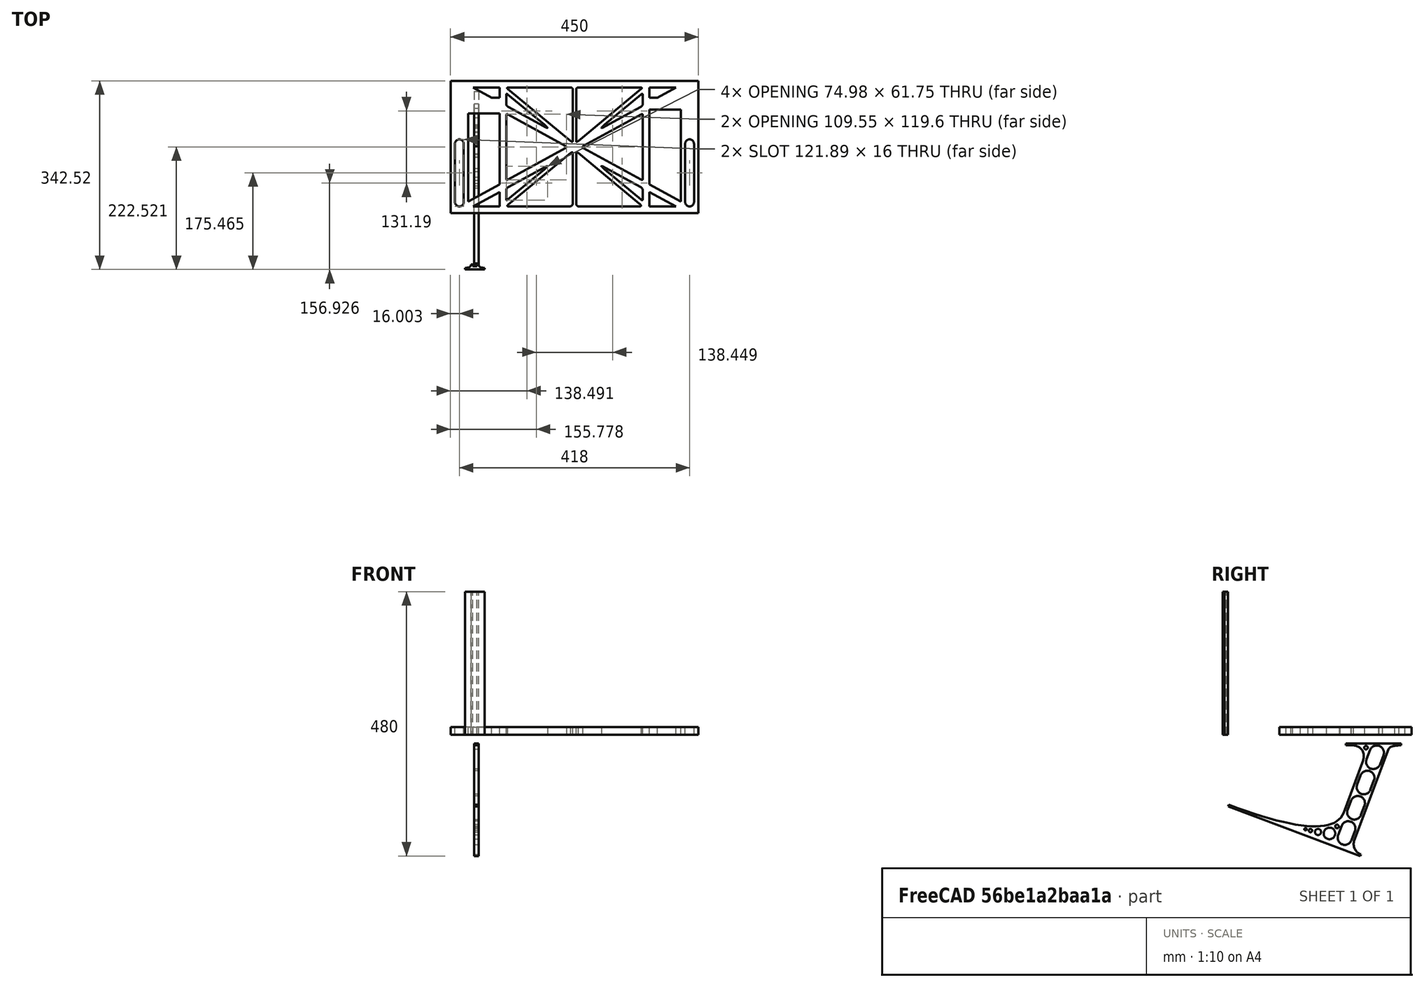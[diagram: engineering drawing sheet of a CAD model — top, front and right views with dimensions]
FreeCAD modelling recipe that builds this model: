
FCSTD DOCUMENT  (FreeCAD 0.19R0.19.2)
Label: laptopStand096
License: All rights reserved
LicenseURL: http://en.wikipedia.org/wiki/All_rights_reserved
objects: Sketcher::SketchObject×3, Part::Extrusion×3
note: 6 computed .brp shape members not serialized (recipe doc carries the construction recipe); baked Part::Feature solids carry a one-line shape summary decoded from their .brp

FEATURE [Sketcher::SketchObject] Sketch
  FullyConstrained = false
  sketch-geometry (252):
    g0: LineSegment StartX=-10.9272 StartY=-82.7794 StartZ=0 EndX=46.0728 EndY=-51.4823 EndZ=0
    g1: LineSegment StartX=366.073 StartY=-91.7794 StartZ=0 EndX=318.073 EndY=-65.424 EndZ=0
    g2: LineSegment StartX=-10.9272 StartY=77.3346 StartZ=0 EndX=-10.9272 EndY=-82.7794 EndZ=0
    g3: LineSegment StartX=375.073 StartY=-82.7794 StartZ=0 EndX=375.073 EndY=83.9235 EndZ=0
    g4: LineSegment StartX=-1.92719 StartY=-91.7794 StartZ=0 EndX=46.0728 EndY=-91.7794 EndZ=0
    g5: LineSegment StartX=318.073 StartY=124.221 StartZ=0 EndX=366.073 EndY=124.221 EndZ=0
    g6: LineSegment StartX=318.073 StartY=83.9235 StartZ=0 EndX=318.073 EndY=-51.4823 EndZ=0
    g7: LineSegment StartX=318.073 StartY=-51.4823 StartZ=0 EndX=375.073 EndY=-82.7794 EndZ=0
    g8: LineSegment StartX=318.073 StartY=-65.424 StartZ=0 EndX=318.073 EndY=-91.7794 EndZ=0
    g9: LineSegment StartX=318.073 StartY=-91.7794 StartZ=0 EndX=366.073 EndY=-91.7794 EndZ=0
    g10: LineSegment StartX=46.0728 StartY=-65.424 StartZ=0 EndX=-1.92719 EndY=-91.7794 EndZ=0
    g11: LineSegment StartX=46.0728 StartY=-65.424 StartZ=0 EndX=46.0728 EndY=-91.7794 EndZ=0
    g12: LineSegment StartX=46.0728 StartY=77.3346 StartZ=0 EndX=46.0728 EndY=-51.4823 EndZ=0
    g13: LineSegment StartX=-42.9272 StartY=136.221 StartZ=0 EndX=-42.9272 EndY=-103.779 EndZ=0
    g14: LineSegment StartX=407.073 StartY=136.221 StartZ=0 EndX=407.073 EndY=-103.779 EndZ=0
    g15: ArcOfCircle CenterX=-26.9272 CenterY=22.1087 CenterZ=0 NormalX=0 NormalY=0 NormalZ=1 AngleXU=0 Radius=8 StartAngle=1e-16 EndAngle=3.14159
    g16: ArcOfCircle CenterX=-26.9272 CenterY=-83.7794 CenterZ=0 NormalX=0 NormalY=0 NormalZ=1 AngleXU=0 Radius=8 StartAngle=3.14159 EndAngle=6.28319
    g17: LineSegment StartX=-34.9272 StartY=22.1087 StartZ=0 EndX=-34.9272 EndY=-83.7794 EndZ=0
    g18: LineSegment StartX=-18.9272 StartY=22.1087 StartZ=0 EndX=-18.9272 EndY=-83.7794 EndZ=0
    g19: ArcOfCircle CenterX=391.073 CenterY=22.1087 CenterZ=0 NormalX=0 NormalY=0 NormalZ=1 AngleXU=0 Radius=8 StartAngle=-4.4e-15 EndAngle=3.14159
    g20: LineSegment StartX=399.073 StartY=22.1087 StartZ=0 EndX=399.073 EndY=-83.7794 EndZ=0
    g21: LineSegment StartX=383.073 StartY=22.1087 StartZ=0 EndX=383.073 EndY=-83.7794 EndZ=0
    g22: ArcOfCircle CenterX=391.073 CenterY=-83.7794 CenterZ=0 NormalX=0 NormalY=0 NormalZ=1 AngleXU=0 Radius=8 StartAngle=3.14159 EndAngle=6.28319
    g23: Circle CenterX=175.022 CenterY=27.0628 CenterZ=0 NormalX=0 NormalY=0 NormalZ=1 AngleXU=0 Radius=1
    g24: Circle CenterX=179.022 CenterY=24.8665 CenterZ=0 NormalX=0 NormalY=0 NormalZ=1 AngleXU=0 Radius=1
    g25: Circle CenterX=179.022 CenterY=27.0628 CenterZ=0 NormalX=0 NormalY=0 NormalZ=1 AngleXU=0 Radius=1
    g26: BSplineCurve PolesCount=3 KnotsCount=2 Degree=2 IsPeriodic=0
    g27: GeomPoint X=175.022 Y=27.0628 Z=0
    g28: GeomPoint X=179.022 Y=27.0628 Z=0
    g29: Circle CenterX=189.124 CenterY=27.0628 CenterZ=0 NormalX=0 NormalY=0 NormalZ=1 AngleXU=0 Radius=1
    g30: Circle CenterX=185.124 CenterY=24.8665 CenterZ=0 NormalX=0 NormalY=0 NormalZ=1 AngleXU=0 Radius=1
    g31: Circle CenterX=185.124 CenterY=27.0628 CenterZ=0 NormalX=0 NormalY=0 NormalZ=1 AngleXU=0 Radius=1
    g32: BSplineCurve PolesCount=3 KnotsCount=2 Degree=2 IsPeriodic=0
    g33: GeomPoint X=189.124 Y=27.0628 Z=0
    g34: GeomPoint X=185.124 Y=27.0628 Z=0
    g35: Circle CenterX=175.022 CenterY=5.37834 CenterZ=0 NormalX=0 NormalY=0 NormalZ=1 AngleXU=0 Radius=1
    g36: Circle CenterX=179.022 CenterY=7.57463 CenterZ=0 NormalX=0 NormalY=0 NormalZ=1 AngleXU=0 Radius=1
    g37: Circle CenterX=179.022 CenterY=5.34704 CenterZ=0 NormalX=0 NormalY=0 NormalZ=1 AngleXU=0 Radius=1
    g38: BSplineCurve PolesCount=3 KnotsCount=2 Degree=2 IsPeriodic=0
    g39: GeomPoint X=175.022 Y=5.37834 Z=0
    g40: GeomPoint X=179.022 Y=5.34704 Z=0
    g41: Circle CenterX=189.124 CenterY=5.37834 CenterZ=0 NormalX=0 NormalY=0 NormalZ=1 AngleXU=0 Radius=1
    g42: Circle CenterX=185.124 CenterY=7.57463 CenterZ=0 NormalX=0 NormalY=0 NormalZ=1 AngleXU=0 Radius=1
    g43: Circle CenterX=185.124 CenterY=5.34704 CenterZ=0 NormalX=0 NormalY=0 NormalZ=1 AngleXU=0 Radius=1
    g44: BSplineCurve PolesCount=3 KnotsCount=2 Degree=2 IsPeriodic=0
    g45: GeomPoint X=189.124 Y=5.37834 Z=0
    g46: GeomPoint X=185.124 Y=5.34704 Z=0
    g47: Circle CenterX=165.871 CenterY=18.1458 CenterZ=0 NormalX=0 NormalY=0 NormalZ=1 AngleXU=0 Radius=1
    g48: Circle CenterX=169.377 CenterY=16.2206 CenterZ=0 NormalX=0 NormalY=0 NormalZ=1 AngleXU=0 Radius=1
    g49: Circle CenterX=165.871 CenterY=14.2954 CenterZ=0 NormalX=0 NormalY=0 NormalZ=1 AngleXU=0 Radius=1
    g50: BSplineCurve PolesCount=3 KnotsCount=2 Degree=2 IsPeriodic=0
    g51: GeomPoint X=165.871 Y=18.1458 Z=0
    g52: GeomPoint X=165.871 Y=14.2954 Z=0
    g53: Circle CenterX=198.275 CenterY=18.1458 CenterZ=0 NormalX=0 NormalY=0 NormalZ=1 AngleXU=0 Radius=1
    g54: Circle CenterX=194.768 CenterY=16.2206 CenterZ=0 NormalX=0 NormalY=0 NormalZ=1 AngleXU=0 Radius=1
    g55: Circle CenterX=198.275 CenterY=14.2954 CenterZ=0 NormalX=0 NormalY=0 NormalZ=1 AngleXU=0 Radius=1
    g56: BSplineCurve PolesCount=3 KnotsCount=2 Degree=2 IsPeriodic=0
    g57: GeomPoint X=198.275 Y=18.1458 Z=0
    g58: GeomPoint X=198.275 Y=14.2954 Z=0
    g59: LineSegment StartX=407.073 StartY=-103.779 StartZ=0 EndX=-42.9272 EndY=-103.779 EndZ=0
    g60: LineSegment StartX=407.073 StartY=136.221 StartZ=0 EndX=-42.9272 EndY=136.221 EndZ=0
    g61: LineSegment StartX=46.0728 StartY=77.3346 StartZ=0 EndX=-10.9272 EndY=77.3346 EndZ=0
    g62: LineSegment StartX=46.0728 StartY=105.865 StartZ=0 EndX=31.5028 EndY=105.865 EndZ=0
    g63: LineSegment StartX=46.0728 StartY=124.221 StartZ=0 EndX=46.0728 EndY=105.865 EndZ=0
    g64: LineSegment StartX=-1.92719 StartY=124.221 StartZ=0 EndX=31.5028 EndY=105.865 EndZ=0
    g65: LineSegment StartX=46.0728 StartY=124.221 StartZ=0 EndX=-1.92719 EndY=124.221 EndZ=0
    g66: LineSegment StartX=318.073 StartY=83.9235 StartZ=0 EndX=375.073 EndY=83.9235 EndZ=0
    g67: Circle CenterX=125.607 CenterY=54.1951 CenterZ=0 NormalX=0 NormalY=0 NormalZ=1 AngleXU=0 Radius=1
    g68: Circle CenterX=139.632 CenterY=46.4944 CenterZ=0 NormalX=0 NormalY=0 NormalZ=1 AngleXU=0 Radius=1
    g69: Circle CenterX=127.326 CenterY=56.7187 CenterZ=0 NormalX=0 NormalY=0 NormalZ=1 AngleXU=0 Radius=1
    g70: BSplineCurve PolesCount=3 KnotsCount=2 Degree=2 IsPeriodic=0
    g71: GeomPoint X=125.607 Y=54.1951 Z=0
    g72: GeomPoint X=127.326 Y=56.7187 Z=0
    g73: Circle CenterX=236.821 CenterY=56.7187 CenterZ=0 NormalX=0 NormalY=0 NormalZ=1 AngleXU=0 Radius=1
    g74: Circle CenterX=224.513 CenterY=46.4944 CenterZ=0 NormalX=0 NormalY=0 NormalZ=1 AngleXU=0 Radius=1
    g75: Circle CenterX=238.538 CenterY=54.1951 CenterZ=0 NormalX=0 NormalY=0 NormalZ=1 AngleXU=0 Radius=1
    g76: BSplineCurve PolesCount=3 KnotsCount=2 Degree=2 IsPeriodic=0
    g77: GeomPoint X=236.821 Y=56.7187 Z=0
    g78: GeomPoint X=238.538 Y=54.1951 Z=0
    g79: Circle CenterX=238.538 CenterY=-21.7539 CenterZ=0 NormalX=0 NormalY=0 NormalZ=1 AngleXU=0 Radius=1
    g80: Circle CenterX=224.513 CenterY=-14.0532 CenterZ=0 NormalX=0 NormalY=0 NormalZ=1 AngleXU=0 Radius=1
    g81: Circle CenterX=236.821 CenterY=-24.2775 CenterZ=0 NormalX=0 NormalY=0 NormalZ=1 AngleXU=0 Radius=1
    g82: BSplineCurve PolesCount=3 KnotsCount=2 Degree=2 IsPeriodic=0
    g83: GeomPoint X=238.538 Y=-21.7539 Z=0
    g84: GeomPoint X=236.821 Y=-24.2775 Z=0
    g85: Circle CenterX=125.607 CenterY=-21.7539 CenterZ=0 NormalX=0 NormalY=0 NormalZ=1 AngleXU=0 Radius=1
    g86: Circle CenterX=139.632 CenterY=-14.0532 CenterZ=0 NormalX=0 NormalY=0 NormalZ=1 AngleXU=0 Radius=1
    g87: Circle CenterX=127.325 CenterY=-24.2775 CenterZ=0 NormalX=0 NormalY=0 NormalZ=1 AngleXU=0 Radius=1
    g88: BSplineCurve PolesCount=3 KnotsCount=2 Degree=2 IsPeriodic=0
    g89: GeomPoint X=125.607 Y=-21.7539 Z=0
    g90: GeomPoint X=127.325 Y=-24.2775 Z=0
    g91: Circle CenterX=302.996 CenterY=111.695 CenterZ=0 NormalX=0 NormalY=0 NormalZ=1 AngleXU=0 Radius=1
    g92: Circle CenterX=306.073 CenterY=114.251 CenterZ=0 NormalX=0 NormalY=0 NormalZ=1 AngleXU=0 Radius=1
    g93: Circle CenterX=306.073 CenterY=110.251 CenterZ=0 NormalX=0 NormalY=0 NormalZ=1 AngleXU=0 Radius=1
    g94: BSplineCurve PolesCount=3 KnotsCount=2 Degree=2 IsPeriodic=0
    g95: GeomPoint X=302.996 Y=111.695 Z=0
    g96: GeomPoint X=306.073 Y=110.251 Z=0
    g97: Circle CenterX=306.073 CenterY=95.2763 CenterZ=0 NormalX=0 NormalY=0 NormalZ=1 AngleXU=0 Radius=1
    g98: Circle CenterX=306.073 CenterY=91.2763 CenterZ=0 NormalX=0 NormalY=0 NormalZ=1 AngleXU=0 Radius=1
    g99: Circle CenterX=302.567 CenterY=89.3511 CenterZ=0 NormalX=0 NormalY=0 NormalZ=1 AngleXU=0 Radius=1
    g100: BSplineCurve PolesCount=3 KnotsCount=2 Degree=2 IsPeriodic=0
    g101: GeomPoint X=306.073 Y=95.2763 Z=0
    g102: GeomPoint X=302.567 Y=89.3511 Z=0
    g103: LineSegment StartX=306.073 StartY=110.251 StartZ=0 EndX=306.073 EndY=95.2763 EndZ=0
    g104: LineSegment StartX=302.996 StartY=111.695 StartZ=0 EndX=236.821 EndY=56.7187 EndZ=0
    g105: LineSegment StartX=238.538 StartY=54.1951 StartZ=0 EndX=302.567 EndY=89.3511 EndZ=0
    g106: Circle CenterX=61.1496 CenterY=111.695 CenterZ=0 NormalX=0 NormalY=0 NormalZ=1 AngleXU=0 Radius=1
    g107: Circle CenterX=58.0728 CenterY=114.251 CenterZ=0 NormalX=0 NormalY=0 NormalZ=1 AngleXU=0 Radius=1
    g108: Circle CenterX=58.0728 CenterY=110.251 CenterZ=0 NormalX=0 NormalY=0 NormalZ=1 AngleXU=0 Radius=1
    g109: BSplineCurve PolesCount=3 KnotsCount=2 Degree=2 IsPeriodic=0
    g110: GeomPoint X=61.1496 Y=111.695 Z=0
    g111: GeomPoint X=58.0728 Y=110.251 Z=0
    g112: Circle CenterX=61.5791 CenterY=89.3511 CenterZ=0 NormalX=0 NormalY=0 NormalZ=1 AngleXU=0 Radius=1
    g113: Circle CenterX=58.0728 CenterY=91.2763 CenterZ=0 NormalX=0 NormalY=0 NormalZ=1 AngleXU=0 Radius=1
    g114: Circle CenterX=58.0728 CenterY=95.2763 CenterZ=0 NormalX=0 NormalY=0 NormalZ=1 AngleXU=0 Radius=1
    g115: BSplineCurve PolesCount=3 KnotsCount=2 Degree=2 IsPeriodic=0
    g116: GeomPoint X=61.5791 Y=89.3511 Z=0
    g117: GeomPoint X=58.0728 Y=95.2763 Z=0
    g118: LineSegment StartX=58.0728 StartY=110.251 StartZ=0 EndX=58.0728 EndY=95.2763 EndZ=0
    g119: LineSegment StartX=61.1496 StartY=111.695 StartZ=0 EndX=127.326 EndY=56.7187 EndZ=0
    g120: LineSegment StartX=125.607 StartY=54.1951 StartZ=0 EndX=61.5791 EndY=89.3511 EndZ=0
    g121: Circle CenterX=61.5791 CenterY=-56.9099 CenterZ=0 NormalX=0 NormalY=0 NormalZ=1 AngleXU=0 Radius=1
    g122: Circle CenterX=58.0728 CenterY=-58.8351 CenterZ=0 NormalX=0 NormalY=0 NormalZ=1 AngleXU=0 Radius=1
    g123: Circle CenterX=58.0728 CenterY=-62.8351 CenterZ=0 NormalX=0 NormalY=0 NormalZ=1 AngleXU=0 Radius=1
    g124: BSplineCurve PolesCount=3 KnotsCount=2 Degree=2 IsPeriodic=0
    g125: GeomPoint X=61.5791 Y=-56.9099 Z=0
    g126: GeomPoint X=58.0728 Y=-62.8351 Z=0
    g127: Circle CenterX=58.0728 CenterY=-77.8102 CenterZ=0 NormalX=0 NormalY=0 NormalZ=1 AngleXU=0 Radius=1
    g128: Circle CenterX=58.0728 CenterY=-81.8102 CenterZ=0 NormalX=0 NormalY=0 NormalZ=1 AngleXU=0 Radius=1
    g129: Circle CenterX=61.1496 CenterY=-79.2541 CenterZ=0 NormalX=0 NormalY=0 NormalZ=1 AngleXU=0 Radius=1
    g130: BSplineCurve PolesCount=3 KnotsCount=2 Degree=2 IsPeriodic=0
    g131: GeomPoint X=58.0728 Y=-77.8102 Z=0
    g132: GeomPoint X=61.1496 Y=-79.2541 Z=0
    g133: LineSegment StartX=58.0728 StartY=-62.8351 StartZ=0 EndX=58.0728 EndY=-77.8102 EndZ=0
    g134: LineSegment StartX=61.1496 StartY=-79.2541 StartZ=0 EndX=127.325 EndY=-24.2775 EndZ=0
    g135: LineSegment StartX=125.607 StartY=-21.7539 StartZ=0 EndX=61.5791 EndY=-56.9099 EndZ=0
    g136: Circle CenterX=302.567 CenterY=-56.9099 CenterZ=0 NormalX=0 NormalY=0 NormalZ=1 AngleXU=0 Radius=1
    g137: Circle CenterX=306.073 CenterY=-58.8351 CenterZ=0 NormalX=0 NormalY=0 NormalZ=1 AngleXU=0 Radius=1
    g138: Circle CenterX=306.073 CenterY=-62.8351 CenterZ=0 NormalX=0 NormalY=0 NormalZ=1 AngleXU=0 Radius=1
    g139: BSplineCurve PolesCount=3 KnotsCount=2 Degree=2 IsPeriodic=0
    g140: GeomPoint X=302.567 Y=-56.9099 Z=0
    g141: GeomPoint X=306.073 Y=-62.8351 Z=0
    g142: Circle CenterX=302.996 CenterY=-79.2541 CenterZ=0 NormalX=0 NormalY=0 NormalZ=1 AngleXU=0 Radius=1
    g143: Circle CenterX=306.073 CenterY=-81.8102 CenterZ=0 NormalX=0 NormalY=0 NormalZ=1 AngleXU=0 Radius=1
    g144: Circle CenterX=306.073 CenterY=-77.8102 CenterZ=0 NormalX=0 NormalY=0 NormalZ=1 AngleXU=0 Radius=1
    g145: BSplineCurve PolesCount=3 KnotsCount=2 Degree=2 IsPeriodic=0
    g146: GeomPoint X=302.996 Y=-79.2541 Z=0
    g147: GeomPoint X=306.073 Y=-77.8102 Z=0
    g148: LineSegment StartX=306.073 StartY=-62.8351 StartZ=0 EndX=306.073 EndY=-77.8102 EndZ=0
    g149: LineSegment StartX=302.996 StartY=-79.2541 StartZ=0 EndX=236.821 EndY=-24.2775 EndZ=0
    g150: LineSegment StartX=238.538 StartY=-21.7539 StartZ=0 EndX=302.567 EndY=-56.9099 EndZ=0
    g151: Circle CenterX=61.6457 CenterY=-88.8112 CenterZ=0 NormalX=0 NormalY=0 NormalZ=1 AngleXU=0 Radius=1
    g152: Circle CenterX=58.0728 CenterY=-91.7794 CenterZ=0 NormalX=0 NormalY=0 NormalZ=1 AngleXU=0 Radius=1
    g153: Circle CenterX=63.9135 CenterY=-91.7794 CenterZ=0 NormalX=0 NormalY=0 NormalZ=1 AngleXU=0 Radius=1
    g154: BSplineCurve PolesCount=3 KnotsCount=2 Degree=2 IsPeriodic=0
    g155: GeomPoint X=61.6457 Y=-88.8112 Z=0
    g156: GeomPoint X=63.9135 Y=-91.7794 Z=0
    g157: Circle CenterX=179.022 CenterY=-85.8163 CenterZ=0 NormalX=0 NormalY=0 NormalZ=1 AngleXU=0 Radius=1
    g158: Circle CenterX=179.022 CenterY=-91.7794 CenterZ=0 NormalX=0 NormalY=0 NormalZ=1 AngleXU=0 Radius=1
    g159: Circle CenterX=171.895 CenterY=-91.7794 CenterZ=0 NormalX=0 NormalY=0 NormalZ=1 AngleXU=0 Radius=1
    g160: BSplineCurve PolesCount=3 KnotsCount=2 Degree=2 IsPeriodic=0
    g161: GeomPoint X=179.022 Y=-85.8163 Z=0
    g162: GeomPoint X=171.895 Y=-91.7794 Z=0
    g163: Circle CenterX=185.124 CenterY=-86.2028 CenterZ=0 NormalX=0 NormalY=0 NormalZ=1 AngleXU=0 Radius=1
    g164: Circle CenterX=185.124 CenterY=-91.7794 CenterZ=0 NormalX=0 NormalY=0 NormalZ=1 AngleXU=0 Radius=1
    g165: Circle CenterX=191.747 CenterY=-91.7794 CenterZ=0 NormalX=0 NormalY=0 NormalZ=1 AngleXU=0 Radius=1
    g166: BSplineCurve PolesCount=3 KnotsCount=2 Degree=2 IsPeriodic=0
    g167: GeomPoint X=185.124 Y=-86.2028 Z=0
    g168: GeomPoint X=191.747 Y=-91.7794 Z=0
    g169: Circle CenterX=299.888 CenterY=-86.6413 CenterZ=0 NormalX=0 NormalY=0 NormalZ=1 AngleXU=0 Radius=1
    g170: Circle CenterX=306.073 CenterY=-91.7794 CenterZ=0 NormalX=0 NormalY=0 NormalZ=1 AngleXU=0 Radius=1
    g171: Circle CenterX=298.776 CenterY=-91.7794 CenterZ=0 NormalX=0 NormalY=0 NormalZ=1 AngleXU=0 Radius=1
    g172: BSplineCurve PolesCount=3 KnotsCount=2 Degree=2 IsPeriodic=0
    g173: GeomPoint X=299.888 Y=-86.6413 Z=0
    g174: GeomPoint X=298.776 Y=-91.7794 Z=0
    g175: LineSegment StartX=189.124 StartY=5.37834 StartZ=0 EndX=299.888 EndY=-86.6413 EndZ=0
    g176: LineSegment StartX=298.776 StartY=-91.7794 StartZ=0 EndX=191.747 EndY=-91.7794 EndZ=0
    g177: LineSegment StartX=185.124 StartY=-86.2028 StartZ=0 EndX=185.124 EndY=5.34704 EndZ=0
    g178: LineSegment StartX=179.022 StartY=5.34704 StartZ=0 EndX=179.022 EndY=-85.8163 EndZ=0
    g179: LineSegment StartX=171.895 StartY=-91.7794 StartZ=0 EndX=63.9135 EndY=-91.7794 EndZ=0
    g180: LineSegment StartX=61.6457 StartY=-88.8112 StartZ=0 EndX=175.022 EndY=5.37834 EndZ=0
    g181: Circle CenterX=302.073 CenterY=124.221 CenterZ=0 NormalX=0 NormalY=0 NormalZ=1 AngleXU=0 Radius=1
    g182: Circle CenterX=306.073 CenterY=124.221 CenterZ=0 NormalX=0 NormalY=0 NormalZ=1 AngleXU=0 Radius=1
    g183: Circle CenterX=302.996 CenterY=121.665 CenterZ=0 NormalX=0 NormalY=0 NormalZ=1 AngleXU=0 Radius=1
    g184: BSplineCurve PolesCount=3 KnotsCount=2 Degree=2 IsPeriodic=0
    g185: GeomPoint X=302.073 Y=124.221 Z=0
    g186: GeomPoint X=302.996 Y=121.665 Z=0
    g187: Circle CenterX=189.124 CenterY=124.221 CenterZ=0 NormalX=0 NormalY=0 NormalZ=1 AngleXU=0 Radius=1
    g188: Circle CenterX=185.124 CenterY=124.221 CenterZ=0 NormalX=0 NormalY=0 NormalZ=1 AngleXU=0 Radius=1
    g189: Circle CenterX=185.124 CenterY=120.221 CenterZ=0 NormalX=0 NormalY=0 NormalZ=1 AngleXU=0 Radius=1
    g190: BSplineCurve PolesCount=3 KnotsCount=2 Degree=2 IsPeriodic=0
    g191: GeomPoint X=189.124 Y=124.221 Z=0
    g192: GeomPoint X=185.124 Y=120.221 Z=0
    g193: Circle CenterX=175.022 CenterY=124.221 CenterZ=0 NormalX=0 NormalY=0 NormalZ=1 AngleXU=0 Radius=1
    g194: Circle CenterX=179.022 CenterY=124.221 CenterZ=0 NormalX=0 NormalY=0 NormalZ=1 AngleXU=0 Radius=1
    g195: Circle CenterX=179.022 CenterY=120.221 CenterZ=0 NormalX=0 NormalY=0 NormalZ=1 AngleXU=0 Radius=1
    g196: BSplineCurve PolesCount=3 KnotsCount=2 Degree=2 IsPeriodic=0
    g197: GeomPoint X=175.022 Y=124.221 Z=0
    g198: GeomPoint X=179.022 Y=120.221 Z=0
    g199: Circle CenterX=62.0728 CenterY=124.221 CenterZ=0 NormalX=0 NormalY=0 NormalZ=1 AngleXU=0 Radius=1
    g200: Circle CenterX=58.0728 CenterY=124.221 CenterZ=0 NormalX=0 NormalY=0 NormalZ=1 AngleXU=0 Radius=1
    g201: Circle CenterX=61.1496 CenterY=121.665 CenterZ=0 NormalX=0 NormalY=0 NormalZ=1 AngleXU=0 Radius=1
    g202: BSplineCurve PolesCount=3 KnotsCount=2 Degree=2 IsPeriodic=0
    g203: GeomPoint X=62.0728 Y=124.221 Z=0
    g204: GeomPoint X=61.1496 Y=121.665 Z=0
    g205: LineSegment StartX=62.0728 StartY=124.221 StartZ=0 EndX=175.022 EndY=124.221 EndZ=0
    g206: LineSegment StartX=179.022 StartY=120.221 StartZ=0 EndX=179.022 EndY=27.0628 EndZ=0
    g207: LineSegment StartX=185.124 StartY=27.0628 StartZ=0 EndX=185.124 EndY=120.221 EndZ=0
    g208: LineSegment StartX=189.124 StartY=124.221 StartZ=0 EndX=302.073 EndY=124.221 EndZ=0
    g209: LineSegment StartX=302.996 StartY=121.665 StartZ=0 EndX=189.124 EndY=27.0628 EndZ=0
    g210: LineSegment StartX=175.022 StartY=27.0628 StartZ=0 EndX=61.1496 EndY=121.665 EndZ=0
    g211: Circle CenterX=61.5791 CenterY=75.4095 CenterZ=0 NormalX=0 NormalY=0 NormalZ=1 AngleXU=0 Radius=1
    g212: Circle CenterX=58.0728 CenterY=77.3346 CenterZ=0 NormalX=0 NormalY=0 NormalZ=1 AngleXU=0 Radius=1
    g213: Circle CenterX=58.0728 CenterY=73.3346 CenterZ=0 NormalX=0 NormalY=0 NormalZ=1 AngleXU=0 Radius=1
    g214: BSplineCurve PolesCount=3 KnotsCount=2 Degree=2 IsPeriodic=0
    g215: GeomPoint X=61.5791 Y=75.4095 Z=0
    g216: GeomPoint X=58.0728 Y=73.3346 Z=0
    g217: Circle CenterX=58.0728 CenterY=-40.8935 CenterZ=0 NormalX=0 NormalY=0 NormalZ=1 AngleXU=0 Radius=1
    g218: Circle CenterX=58.0728 CenterY=-44.8935 CenterZ=0 NormalX=0 NormalY=0 NormalZ=1 AngleXU=0 Radius=1
    g219: Circle CenterX=61.5791 CenterY=-42.9683 CenterZ=0 NormalX=0 NormalY=0 NormalZ=1 AngleXU=0 Radius=1
    g220: BSplineCurve PolesCount=3 KnotsCount=2 Degree=2 IsPeriodic=0
    g221: GeomPoint X=58.0728 Y=-40.8935 Z=0
    g222: GeomPoint X=61.5791 Y=-42.9683 Z=0
    g223: LineSegment StartX=61.5791 StartY=-42.9683 StartZ=0 EndX=165.871 EndY=14.2954 EndZ=0
    g224: LineSegment StartX=165.871 StartY=18.1458 StartZ=0 EndX=61.5791 EndY=75.4095 EndZ=0
    g225: LineSegment StartX=58.0728 StartY=73.3346 StartZ=0 EndX=58.0728 EndY=-40.8935 EndZ=0
    g226: Circle CenterX=302.567 CenterY=-42.9683 CenterZ=0 NormalX=0 NormalY=0 NormalZ=1 AngleXU=0 Radius=1
    g227: Circle CenterX=306.073 CenterY=-44.8935 CenterZ=0 NormalX=0 NormalY=0 NormalZ=1 AngleXU=0 Radius=1
    g228: Circle CenterX=306.073 CenterY=-40.8935 CenterZ=0 NormalX=0 NormalY=0 NormalZ=1 AngleXU=0 Radius=1
    g229: BSplineCurve PolesCount=3 KnotsCount=2 Degree=2 IsPeriodic=0
    g230: GeomPoint X=302.567 Y=-42.9683 Z=0
    g231: GeomPoint X=306.073 Y=-40.8935 Z=0
    g232: Circle CenterX=306.073 CenterY=73.3346 CenterZ=0 NormalX=0 NormalY=0 NormalZ=1 AngleXU=0 Radius=1
    g233: Circle CenterX=306.073 CenterY=77.3346 CenterZ=0 NormalX=0 NormalY=0 NormalZ=1 AngleXU=0 Radius=1
    g234: Circle CenterX=302.567 CenterY=75.4095 CenterZ=0 NormalX=0 NormalY=0 NormalZ=1 AngleXU=0 Radius=1
    g235: BSplineCurve PolesCount=3 KnotsCount=2 Degree=2 IsPeriodic=0
    g236: GeomPoint X=306.073 Y=73.3346 Z=0
    g237: GeomPoint X=302.567 Y=75.4095 Z=0
    g238: LineSegment StartX=302.567 StartY=-42.9683 StartZ=0 EndX=198.275 EndY=14.2954 EndZ=0
    g239: LineSegment StartX=198.275 StartY=18.1458 StartZ=0 EndX=302.567 EndY=75.4095 EndZ=0
    g240: LineSegment StartX=306.073 StartY=73.3346 StartZ=0 EndX=306.073 EndY=-40.8935 EndZ=0
    g241: LineSegment StartX=318.073 StartY=124.221 StartZ=0 EndX=322.073 EndY=124.221 EndZ=0
    g242: LineSegment StartX=366.073 StartY=124.221 StartZ=0 EndX=362.073 EndY=124.221 EndZ=0
    g243: LineSegment StartX=328.643 StartY=105.865 StartZ=0 EndX=332.643 EndY=105.865 EndZ=0
    g244: LineSegment StartX=335.875 StartY=105.45 StartZ=0 EndX=339.381 EndY=107.376 EndZ=0
    g245: LineSegment StartX=367.034 StartY=122.717 StartZ=0 EndX=363.529 EndY=120.79 EndZ=0
    g246: LineSegment StartX=318.073 StartY=105.865 StartZ=0 EndX=318.073 EndY=109.865 EndZ=0
    g247: LineSegment StartX=318.073 StartY=105.865 StartZ=0 EndX=322.073 EndY=105.865 EndZ=0
    g248: LineSegment StartX=318.073 StartY=124.221 StartZ=0 EndX=318.073 EndY=120.221 EndZ=0
    g249: LineSegment StartX=332.651 StartY=105.853 StartZ=0 EndX=366.073 EndY=124.221 EndZ=0
    g250: LineSegment StartX=322.073 StartY=105.865 StartZ=0 EndX=328.643 EndY=105.865 EndZ=0
    g251: LineSegment StartX=318.073 StartY=120.221 StartZ=0 EndX=318.073 EndY=109.865 EndZ=0
  constraints (433):
    c: Horizontal(g4)
    c: Coincident(g6,g7)
    c: Coincident(g8,g1)
    c: Tangent(g6,g8)
    c: Coincident(g11,g10)
    c: Coincident(g0,g12)
    c: Block(g7)
    c: Block(g3)
    c: Block(g1)
    c: Block(g8)
    c: Block(g11)
    c: Block(g10)
    c: Block(g0)
    c: Block(g2)
    c: Block(g5)
    c: Block(g9)
    c: Block(g4)
    c: Vertical(g13)
    c: Vertical(g14)
    c: Block(g14)
    c: Block(g13)
    c: Tangent(g15,g18) = 1.5708
    c: Tangent(g15,g17) = -1.5708
    c: Tangent(g17,g16) = -1.5708
    c: Tangent(g18,g16) = 1.5708
    c: Vertical(g17)
    c: Equal(g15,g16)
    c: Block(g18)
    c: Block(g17)
    c: Tangent(g19,g20) = 1.5708
    c: Tangent(g20,g22) = 1.5708
    c: Equal(g19,g22)
    c: Coincident(g21,g19)
    c: Coincident(g21,g22)
    c: Block(g20)
    c: Block(g21)
    c: Weight(g23) = 1
    c: Equal(g23,g24)
    c: Equal(g23,g25)
    c: InternalAlignment(g23,g26)
    c: InternalAlignment(g24,g26)
    c: InternalAlignment(g25,g26)
    c: InternalAlignment(g27,g26)
    c: InternalAlignment(g28,g26)
    c: Weight(g29) = 1
    c: Equal(g29,g30)
    c: Equal(g29,g31)
    c: InternalAlignment(g29,g32)
    c: InternalAlignment(g30,g32)
    c: InternalAlignment(g31,g32)
    c: InternalAlignment(g33,g32)
    c: InternalAlignment(g34,g32)
    c: Block(g32)
    c: Block(g26)
    c: Weight(g35) = 1
    c: Equal(g35,g36)
    c: Equal(g35,g37)
    c: InternalAlignment(g35,g38)
    c: InternalAlignment(g36,g38)
    c: InternalAlignment(g37,g38)
    c: InternalAlignment(g39,g38)
    c: InternalAlignment(g40,g38)
    c: Weight(g41) = 1
    c: Equal(g41,g42)
    c: Equal(g41,g43)
    c: InternalAlignment(g41,g44)
    c: InternalAlignment(g42,g44)
    c: InternalAlignment(g43,g44)
    c: InternalAlignment(g45,g44)
    c: InternalAlignment(g46,g44)
    c: Block(g44)
    c: Block(g38)
    c: Weight(g47) = 1
    c: Equal(g47,g48)
    c: Equal(g47,g49)
    c: InternalAlignment(g47,g50)
    c: InternalAlignment(g48,g50)
    c: InternalAlignment(g49,g50)
    c: InternalAlignment(g51,g50)
    c: InternalAlignment(g52,g50)
    c: Weight(g53) = 1
    c: Equal(g53,g54)
    c: Equal(g53,g55)
    c: InternalAlignment(g53,g56)
    c: InternalAlignment(g54,g56)
    c: InternalAlignment(g55,g56)
    c: InternalAlignment(g57,g56)
    c: InternalAlignment(g58,g56)
    c: Block(g50)
    c: Block(g56)
    c: Coincident(g59,g14)
    c: Coincident(g59,g13)
    c: Horizontal(g59)
    c: Distance(g59) = 450
    c: Coincident(g60,g14)
    c: Coincident(g60,g13)
    c: Horizontal(g60)
    c: Horizontal(g61)
    c: Coincident(g12,g61)
    c: Horizontal(g62)
    c: Vertical(g63)
    c: Block(g63)
    c: Block(g62)
    c: Block(g61)
    c: Distance(g63) = 18.3554
    c: Coincident(g65,g63)
    c: Coincident(g65,g64)
    c: Horizontal(g65)
    c: Block(g65)
    c: Block(g64)
    c: Coincident(g62,g64)
    c: Coincident(g2,g61)
    c: Coincident(g66,g6)
    c: Horizontal(g66)
    c: Block(g66)
    c: Coincident(g3,g66)
    c: Weight(g67) = 1
    c: Equal(g67,g68)
    c: Equal(g67,g69)
    c: InternalAlignment(g67,g70)
    c: InternalAlignment(g68,g70)
    c: InternalAlignment(g69,g70)
    c: InternalAlignment(g71,g70)
    c: InternalAlignment(g72,g70)
    c: Block(g70)
    c: Weight(g73) = 1
    c: Equal(g73,g74)
    c: Equal(g73,g75)
    c: InternalAlignment(g73,g76)
    c: InternalAlignment(g74,g76)
    c: InternalAlignment(g75,g76)
    c: InternalAlignment(g77,g76)
    c: InternalAlignment(g78,g76)
    c: Block(g76)
    c: Weight(g79) = 1
    c: Equal(g79,g80)
    c: Equal(g79,g81)
    c: InternalAlignment(g79,g82)
    c: InternalAlignment(g80,g82)
    c: InternalAlignment(g81,g82)
    c: InternalAlignment(g83,g82)
    c: InternalAlignment(g84,g82)
    c: Block(g82)
    c: Weight(g85) = 1
    c: Equal(g85,g86)
    c: Equal(g85,g87)
    c: InternalAlignment(g85,g88)
    c: InternalAlignment(g86,g88)
    c: InternalAlignment(g87,g88)
    c: InternalAlignment(g89,g88)
    c: InternalAlignment(g90,g88)
    c: Block(g88)
    c: Weight(g91) = 1
    c: Equal(g91,g92)
    c: Equal(g91,g93)
    c: InternalAlignment(g91,g94)
    c: InternalAlignment(g92,g94)
    c: InternalAlignment(g93,g94)
    c: InternalAlignment(g95,g94)
    c: InternalAlignment(g96,g94)
    c: Weight(g97) = 1
    c: Equal(g97,g98)
    c: Equal(g97,g99)
    c: InternalAlignment(g97,g100)
    c: InternalAlignment(g98,g100)
    c: InternalAlignment(g99,g100)
    c: InternalAlignment(g101,g100)
    c: InternalAlignment(g102,g100)
    c: Block(g94)
    c: Block(g100)
    c: Coincident(g103,g94)
    c: Coincident(g103,g100)
    c: Vertical(g103)
    c: Coincident(g104,g94)
    c: Coincident(g104,g76)
    c: Coincident(g105,g76)
    c: Coincident(g105,g100)
    c: Weight(g106) = 1
    c: Equal(g106,g107)
    c: Equal(g106,g108)
    c: InternalAlignment(g106,g109)
    c: InternalAlignment(g107,g109)
    c: InternalAlignment(g108,g109)
    c: InternalAlignment(g110,g109)
    c: InternalAlignment(g111,g109)
    c: Weight(g112) = 1
    c: Equal(g112,g113)
    c: Equal(g112,g114)
    c: InternalAlignment(g112,g115)
    c: InternalAlignment(g113,g115)
    c: InternalAlignment(g114,g115)
    c: InternalAlignment(g116,g115)
    c: InternalAlignment(g117,g115)
    c: Block(g109)
    c: Block(g115)
    c: Coincident(g118,g109)
    c: Coincident(g118,g115)
    c: Vertical(g118)
    c: Coincident(g119,g109)
    c: Coincident(g119,g70)
    c: Coincident(g120,g70)
    c: Coincident(g120,g115)
    c: Weight(g121) = 1
    c: Equal(g121,g122)
    c: Equal(g121,g123)
    c: InternalAlignment(g121,g124)
    c: InternalAlignment(g122,g124)
    c: InternalAlignment(g123,g124)
    c: InternalAlignment(g125,g124)
    c: InternalAlignment(g126,g124)
    c: Weight(g127) = 1
    c: Equal(g127,g128)
    c: Equal(g127,g129)
    c: InternalAlignment(g127,g130)
    c: InternalAlignment(g128,g130)
    c: InternalAlignment(g129,g130)
    c: InternalAlignment(g131,g130)
    c: InternalAlignment(g132,g130)
    c: Block(g124)
    c: Block(g130)
    c: Coincident(g133,g124)
    c: Coincident(g133,g130)
    c: Vertical(g133)
    c: Coincident(g134,g130)
    c: Coincident(g134,g88)
    c: Coincident(g135,g88)
    c: Coincident(g135,g124)
    c: Weight(g136) = 1
    c: Equal(g136,g137)
    c: Equal(g136,g138)
    c: InternalAlignment(g136,g139)
    c: InternalAlignment(g137,g139)
    c: InternalAlignment(g138,g139)
    c: InternalAlignment(g140,g139)
    c: InternalAlignment(g141,g139)
    c: Weight(g142) = 1
    c: Equal(g142,g143)
    c: Equal(g142,g144)
    c: InternalAlignment(g142,g145)
    c: InternalAlignment(g143,g145)
    c: InternalAlignment(g144,g145)
    c: InternalAlignment(g146,g145)
    c: InternalAlignment(g147,g145)
    c: Block(g139)
    c: Block(g145)
    c: Coincident(g148,g139)
    c: Coincident(g148,g145)
    c: Vertical(g148)
    c: Coincident(g149,g145)
    c: Coincident(g149,g82)
    c: Coincident(g150,g82)
    c: Coincident(g150,g139)
    c: Weight(g151) = 1
    c: Equal(g151,g152)
    c: Equal(g151,g153)
    c: InternalAlignment(g151,g154)
    c: InternalAlignment(g152,g154)
    c: InternalAlignment(g153,g154)
    c: InternalAlignment(g155,g154)
    c: InternalAlignment(g156,g154)
    c: Weight(g157) = 1
    c: Equal(g157,g158)
    c: Equal(g157,g159)
    c: InternalAlignment(g157,g160)
    c: InternalAlignment(g158,g160)
    c: InternalAlignment(g159,g160)
    c: InternalAlignment(g161,g160)
    c: InternalAlignment(g162,g160)
    c: Weight(g163) = 1
    c: Equal(g163,g164)
    c: Equal(g163,g165)
    c: InternalAlignment(g163,g166)
    c: InternalAlignment(g164,g166)
    c: InternalAlignment(g165,g166)
    c: InternalAlignment(g167,g166)
    c: InternalAlignment(g168,g166)
    c: Weight(g169) = 1
    c: Equal(g169,g170)
    c: Equal(g169,g171)
    c: InternalAlignment(g169,g172)
    c: InternalAlignment(g170,g172)
    c: InternalAlignment(g171,g172)
    c: InternalAlignment(g173,g172)
    c: InternalAlignment(g174,g172)
    c: Block(g172)
    c: Block(g166)
    c: Block(g160)
    c: Block(g154)
    c: Coincident(g175,g44)
    c: Coincident(g175,g172)
    c: Coincident(g176,g172)
    c: Coincident(g176,g166)
    c: Horizontal(g176)
    c: Coincident(g177,g166)
    c: Coincident(g177,g44)
    c: Vertical(g177)
    c: Coincident(g178,g38)
    c: Coincident(g178,g160)
    c: Vertical(g178)
    c: Coincident(g179,g160)
    c: Coincident(g179,g154)
    c: Horizontal(g179)
    c: Coincident(g180,g154)
    c: Coincident(g180,g38)
    c: Weight(g181) = 1
    c: Equal(g181,g182)
    c: Equal(g181,g183)
    c: InternalAlignment(g181,g184)
    c: InternalAlignment(g182,g184)
    c: InternalAlignment(g183,g184)
    c: InternalAlignment(g185,g184)
    c: InternalAlignment(g186,g184)
    c: Weight(g187) = 1
    c: Equal(g187,g188)
    c: Equal(g187,g189)
    c: InternalAlignment(g187,g190)
    c: InternalAlignment(g188,g190)
    c: InternalAlignment(g189,g190)
    c: InternalAlignment(g191,g190)
    c: InternalAlignment(g192,g190)
    c: Weight(g193) = 1
    c: Equal(g193,g194)
    c: Equal(g193,g195)
    c: InternalAlignment(g193,g196)
    c: InternalAlignment(g194,g196)
    c: InternalAlignment(g195,g196)
    c: InternalAlignment(g197,g196)
    c: InternalAlignment(g198,g196)
    c: Weight(g199) = 1
    c: Equal(g199,g200)
    c: Equal(g199,g201)
    c: InternalAlignment(g199,g202)
    c: InternalAlignment(g200,g202)
    c: InternalAlignment(g201,g202)
    c: InternalAlignment(g203,g202)
    c: InternalAlignment(g204,g202)
    c: Block(g202)
    c: Block(g196)
    c: Block(g190)
    c: Block(g184)
    c: Coincident(g205,g202)
    c: Coincident(g205,g196)
    c: Horizontal(g205)
    c: Coincident(g206,g196)
    c: Coincident(g206,g26)
    c: Vertical(g206)
    c: Coincident(g207,g32)
    c: Coincident(g207,g190)
    c: Vertical(g207)
    c: Coincident(g208,g190)
    c: Coincident(g208,g184)
    c: Horizontal(g208)
    c: Coincident(g209,g184)
    c: Coincident(g209,g32)
    c: Coincident(g210,g26)
    c: Weight(g211) = 1
    c: Equal(g211,g212)
    c: Equal(g211,g213)
    c: InternalAlignment(g211,g214)
    c: InternalAlignment(g212,g214)
    c: InternalAlignment(g213,g214)
    c: InternalAlignment(g215,g214)
    c: InternalAlignment(g216,g214)
    c: Weight(g217) = 1
    c: Equal(g217,g218)
    c: Equal(g217,g219)
    c: InternalAlignment(g217,g220)
    c: InternalAlignment(g218,g220)
    c: InternalAlignment(g219,g220)
    c: InternalAlignment(g221,g220)
    c: InternalAlignment(g222,g220)
    c: Block(g220)
    c: Block(g214)
    c: Coincident(g223,g220)
    c: Coincident(g223,g50)
    c: Coincident(g224,g50)
    c: Coincident(g224,g214)
    c: Coincident(g225,g214)
    c: Coincident(g225,g220)
    c: Vertical(g225)
    c: Weight(g226) = 1
    c: Equal(g226,g227)
    c: Equal(g226,g228)
    c: InternalAlignment(g226,g229)
    c: InternalAlignment(g227,g229)
    c: InternalAlignment(g228,g229)
    c: InternalAlignment(g230,g229)
    c: InternalAlignment(g231,g229)
    c: Weight(g232) = 1
    c: Equal(g232,g233)
    c: Equal(g232,g234)
    c: InternalAlignment(g232,g235)
    c: InternalAlignment(g233,g235)
    c: InternalAlignment(g234,g235)
    c: InternalAlignment(g236,g235)
    c: InternalAlignment(g237,g235)
    c: Block(g235)
    c: Block(g229)
    c: Coincident(g238,g229)
    c: Coincident(g238,g56)
    c: Coincident(g239,g56)
    c: Coincident(g239,g235)
    c: Coincident(g240,g235)
    c: Coincident(g240,g229)
    c: Vertical(g240)
    c: Horizontal(g241)
    c: Horizontal(g242)
    c: Horizontal(g243)
    c: Vertical(g246)
    c: Horizontal(g247)
    c: Vertical(g248)
    c: Distance(g243) = 4
    c: Distance(g247) = 4
    c: Distance(g246) = 4
    c: Distance(g248) = 4
    c: Distance(g241) = 4
    c: Distance(g242) = 4
    c: Coincident(g241,g5)
    c: Coincident(g248,g5)
    c: Coincident(g5,g242)
    c: Coincident(g249,g5)
    c: Coincident(g250,g247)
    c: Coincident(g250,g243)
    c: Horizontal(g250)
    c: Block(g250)
    c: Coincident(g251,g248)
    c: Coincident(g251,g246)
    c: Vertical(g251)
    c: Block(g251)
    c: Distance(g244) = 4
    c: Distance(g245) = 4
    c: Parallel(g244,g249)
    c: Parallel(g245,g249)
FEATURE [Sketcher::SketchObject] Sketch001
  FullyConstrained = true
  MapMode = 4
  Placement = pos=(0,0,0) rot=(0.57735,0.57735,0.57735;2.0944rad)
  Support = -> [Sketch]
  sketch-geometry (46):
    g0: BSplineCurve PolesCount=3 KnotsCount=2 Degree=2 IsPeriodic=0
    g1: ArcOfCircle CenterX=73.1223 CenterY=-32.291 CenterZ=0 NormalX=0 NormalY=0 NormalZ=1 AngleXU=0 Radius=13 StartAngle=5.92268 EndAngle=9.06428
    g2: ArcOfCircle CenterX=66.7816 CenterY=-49.1439 CenterZ=0 NormalX=0 NormalY=0 NormalZ=1 AngleXU=0 Radius=13 StartAngle=2.78068 EndAngle=5.92131
    g3: ArcOfCircle CenterX=55.9263 CenterY=-78.1807 CenterZ=0 NormalX=0 NormalY=0 NormalZ=1 AngleXU=0 Radius=13 StartAngle=5.92268 EndAngle=9.06428
    g4: ArcOfCircle CenterX=49.5884 CenterY=-95.0342 CenterZ=0 NormalX=0 NormalY=0 NormalZ=1 AngleXU=0 Radius=13 StartAngle=2.78068 EndAngle=5.92131
    g5: ArcOfCircle CenterX=38.7206 CenterY=-124.067 CenterZ=0 NormalX=0 NormalY=0 NormalZ=1 AngleXU=0 Radius=13 StartAngle=5.92268 EndAngle=9.06428
    g6: ArcOfCircle CenterX=32.3875 CenterY=-140.92 CenterZ=0 NormalX=0 NormalY=0 NormalZ=1 AngleXU=0 Radius=13 StartAngle=2.78068 EndAngle=5.92131
    g7: ArcOfCircle CenterX=21.4715 CenterY=-169.934 CenterZ=0 NormalX=0 NormalY=0 NormalZ=1 AngleXU=0 Radius=13 StartAngle=5.92268 EndAngle=9.06428
    g8: ArcOfCircle CenterX=15.1336 CenterY=-186.787 CenterZ=0 NormalX=0 NormalY=0 NormalZ=1 AngleXU=0 Radius=13 StartAngle=2.78068 EndAngle=5.92131
    g9-g12: Circle x4 (B-spline internal-alignment scaffolding for g13; pole/knot coordinates omitted)
    g13: BSplineCurve PolesCount=4 KnotsCount=2 Degree=3 IsPeriodic=0
    g14: GeomPoint X=28.8094 Y=-19.0875 Z=0
    g15: GeomPoint X=47.0443 Y=-50.4712 Z=0
    g16: Circle CenterX=53.5586 CenterY=-23.2695 CenterZ=0 NormalX=0 NormalY=0 NormalZ=1 AngleXU=0 Radius=3.24518
    g17: Circle CenterX=-195.441 CenterY=-127.082 CenterZ=0 NormalX=0 NormalY=0 NormalZ=1 AngleXU=0 Radius=1
    g18: Circle CenterX=-8.24091 CenterY=-197.481 CenterZ=0 NormalX=0 NormalY=0 NormalZ=1 AngleXU=0 Radius=1
    g19: Circle CenterX=12.8789 CenterY=-141.321 CenterZ=0 NormalX=0 NormalY=0 NormalZ=1 AngleXU=0 Radius=1
    g20: BSplineCurve PolesCount=3 KnotsCount=2 Degree=2 IsPeriodic=0
    g21: GeomPoint X=-195.441 Y=-127.082 Z=0
    g22: GeomPoint X=12.8789 Y=-141.321 Z=0
    g23: Circle CenterX=-12.8016 CenterY=-179.036 CenterZ=0 NormalX=0 NormalY=0 NormalZ=1 AngleXU=0 Radius=10.5072
    g24: Circle CenterX=0.933922 CenterY=-166.43 CenterZ=0 NormalX=0 NormalY=0 NormalZ=1 AngleXU=0 Radius=3.26661
    g25: Circle CenterX=-33.5518 CenterY=-176.44 CenterZ=0 NormalX=0 NormalY=0 NormalZ=1 AngleXU=0 Radius=5.64388
    g26: Circle CenterX=-47.2366 CenterY=-173.859 CenterZ=0 NormalX=0 NormalY=0 NormalZ=1 AngleXU=0 Radius=3.01653
    g27: Circle CenterX=-56.2595 CenterY=-171.456 CenterZ=0 NormalX=0 NormalY=0 NormalZ=1 AngleXU=0 Radius=2.12826
    g28: ArcOfCircle CenterX=51.2151 CenterY=-198.473 CenterZ=0 NormalX=0 NormalY=0 NormalZ=1 AngleXU=0 Radius=20 StartAngle=2.78189 EndAngle=4.35269
    g29: LineSegment StartX=32.4951 StartY=-191.433 StartZ=0 EndX=94.6578 EndY=-26.1352 EndZ=0
    g30: LineSegment StartX=43.1192 StartY=-220.001 StartZ=0 EndX=-196.497 EndY=-129.89 EndZ=0
    g31: LineSegment StartX=43.1192 StartY=-220.001 StartZ=0 EndX=44.1752 EndY=-217.193 EndZ=0
    g32: LineSegment StartX=117.223 StartY=-19.0875 StartZ=0 EndX=117.223 EndY=-16.0875 EndZ=0
    g33: LineSegment StartX=117.223 StartY=-16.0875 StartZ=0 EndX=17.2232 EndY=-16.0875 EndZ=0
    g34: LineSegment StartX=17.2232 StartY=-16.0875 StartZ=0 EndX=17.2232 EndY=-19.0875 EndZ=0
    g35: LineSegment StartX=28.8094 StartY=-19.0875 StartZ=0 EndX=17.2232 EndY=-19.0875 EndZ=0
    g36: LineSegment StartX=47.0443 StartY=-50.4712 StartZ=0 EndX=12.8789 EndY=-141.321 EndZ=0
    g37: LineSegment StartX=-195.441 StartY=-127.082 StartZ=0 EndX=-196.497 EndY=-129.89 EndZ=0
    g38: LineSegment StartX=85.2866 StartY=-36.8766 StartZ=0 EndX=78.9396 EndY=-53.7463 EndZ=0
    g39: LineSegment StartX=60.9579 StartY=-27.7053 StartZ=0 EndX=54.6191 EndY=-44.5532 EndZ=0
    g40: LineSegment StartX=68.0907 StartY=-82.7664 StartZ=0 EndX=61.7465 EndY=-99.6365 EndZ=0
    g41: LineSegment StartX=43.7619 StartY=-73.595 StartZ=0 EndX=37.426 EndY=-90.4435 EndZ=0
    g42: LineSegment StartX=50.885 StartY=-128.652 StartZ=0 EndX=44.5456 EndY=-145.522 EndZ=0
    g43: LineSegment StartX=26.5562 StartY=-119.481 StartZ=0 EndX=20.2251 EndY=-136.329 EndZ=0
    g44: LineSegment StartX=9.3071 StartY=-165.349 StartZ=0 EndX=2.97115 EndY=-182.197 EndZ=0
    g45: LineSegment StartX=33.6358 StartY=-174.52 StartZ=0 EndX=27.2917 EndY=-191.39 EndZ=0
  constraints (71):
    c: Block(g0)
    c: Block(g1)
    c: Block(g2)
    c: Block(g4)
    c: Block(g3)
    c: Block(g6)
    c: Block(g5)
    c: Block(g8)
    c: Block(g7)
    c: Weight(g9) = 1
    c: Equal(g9,g10)
    c: Equal(g9,g11)
    c: Equal(g9,g12)
    c: InternalAlignment(g9-g12 -> g13) x4
    c: InternalAlignment(g14,g13)
    c: InternalAlignment(g15,g13)
    c: Block(g16)
    c: Weight(g17) = 1
    c: Equal(g17,g18)
    c: Equal(g17,g19)
    c: InternalAlignment(g17,g20)
    c: InternalAlignment(g18,g20)
    c: InternalAlignment(g19,g20)
    c: InternalAlignment(g21,g20)
    c: InternalAlignment(g22,g20)
    c: Block(g20)
    c: Block(g23)
    c: Block(g24)
    c: Block(g25)
    c: Block(g26)
    c: Block(g27)
    c: Block(g28)
    c: Coincident(g29,g28)
    c: Coincident(g29,g0)
    c: Block(g13)
    c: Coincident(g31,g30)
    c: Coincident(g31,g28)
    c: Block(g31)
    c: Coincident(g32,g0)
    c: Vertical(g32)
    c: Coincident(g33,g32)
    c: Horizontal(g33)
    c: Coincident(g34,g33)
    c: Vertical(g34)
    c: Block(g33)
    c: Coincident(g35,g13)
    c: Coincident(g35,g34)
    c: Horizontal(g35)
    c: Coincident(g36,g13)
    c: Coincident(g36,g20)
    c: Coincident(g37,g20)
    c: Coincident(g37,g30)
    c: Block(g30)
    c: Coincident(g38,g1)
    c: Coincident(g38,g2)
    c: Coincident(g39,g1)
    c: Coincident(g39,g2)
    c: Coincident(g40,g3)
    c: Coincident(g40,g4)
    c: Coincident(g41,g3)
    c: Coincident(g41,g4)
    c: Coincident(g42,g5)
    c: Coincident(g42,g6)
    c: Coincident(g43,g5)
    c: Coincident(g43,g6)
    c: Coincident(g44,g7)
    c: Coincident(g44,g8)
    c: Coincident(g45,g7)
    c: Coincident(g45,g8)
    c: Distance(g30) = 256
    c: Distance(g33) = 100
FEATURE [Part::Extrusion] Extrude002
  Base = -> Sketch001
  Dir = (1,0,0)
  DirMode = 2
  FaceMakerClass = Part::FaceMakerBullseye
  LengthFwd = 8
  LengthRev = 0
  Solid = true
  Symmetric = false
FEATURE [Sketcher::SketchObject] Sketch002
  FullyConstrained = true
  sketch-geometry (20):
    g0: LineSegment StartX=-2.77179 StartY=-200.304 StartZ=0 EndX=5.22821 EndY=-200.304 EndZ=0
    g1: LineSegment StartX=5.22821 StartY=-200.304 StartZ=0 EndX=5.22821 EndY=-197.304 EndZ=0
    g2: LineSegment StartX=-2.77179 StartY=-200.304 StartZ=0 EndX=-2.77179 EndY=-197.304 EndZ=0
    g3: LineSegment StartX=5.22821 StartY=-197.304 StartZ=0 EndX=8.22821 EndY=-197.304 EndZ=0
    g4: LineSegment StartX=-2.77179 StartY=-197.304 StartZ=0 EndX=-5.77179 EndY=-197.304 EndZ=0
    g5: LineSegment StartX=19.2282 StartY=-203.304 StartZ=0 EndX=19.2282 EndY=-206.304 EndZ=0
    g6: LineSegment StartX=-16.7718 StartY=-203.304 StartZ=0 EndX=-16.7718 EndY=-206.304 EndZ=0
    g7: LineSegment StartX=-16.7718 StartY=-206.304 StartZ=0 EndX=19.2282 EndY=-206.304 EndZ=0
    g8: Circle CenterX=-16.7718 CenterY=-203.304 CenterZ=0 NormalX=0 NormalY=0 NormalZ=1 AngleXU=0 Radius=1
    g9: Circle CenterX=-5.77179 CenterY=-203.304 CenterZ=0 NormalX=0 NormalY=0 NormalZ=1 AngleXU=0 Radius=1
    g10: Circle CenterX=-5.77179 CenterY=-197.304 CenterZ=0 NormalX=0 NormalY=0 NormalZ=1 AngleXU=0 Radius=1
    g11: BSplineCurve PolesCount=3 KnotsCount=2 Degree=2 IsPeriodic=0
    g12: GeomPoint X=-16.7718 Y=-203.304 Z=0
    g13: GeomPoint X=-5.77179 Y=-197.304 Z=0
    g14: Circle CenterX=19.2282 CenterY=-203.304 CenterZ=0 NormalX=0 NormalY=0 NormalZ=1 AngleXU=0 Radius=1
    g15: Circle CenterX=8.22821 CenterY=-203.304 CenterZ=0 NormalX=0 NormalY=0 NormalZ=1 AngleXU=0 Radius=1
    g16: Circle CenterX=8.22821 CenterY=-197.304 CenterZ=0 NormalX=0 NormalY=0 NormalZ=1 AngleXU=0 Radius=1
    g17: BSplineCurve PolesCount=3 KnotsCount=2 Degree=2 IsPeriodic=0
    g18: GeomPoint X=19.2282 Y=-203.304 Z=0
    g19: GeomPoint X=8.22821 Y=-197.304 Z=0
  constraints (41):
    c: Horizontal(g0)
    c: Distance(g0) = 8
    c: Coincident(g1,g0)
    c: Vertical(g1)
    c: Distance(g1) = 3
    c: Coincident(g2,g0)
    c: Vertical(g2)
    c: Distance(g2) = 3
    c: Coincident(g3,g1)
    c: Horizontal(g3)
    c: Distance(g3) = 3
    c: Coincident(g4,g2)
    c: Horizontal(g4)
    c: Distance(g4) = 3
    c: Vertical(g5)
    c: Vertical(g6)
    c: Coincident(g7,g6)
    c: Coincident(g7,g5)
    c: Weight(g8) = 1
    c: Equal(g8,g9)
    c: Equal(g8,g10)
    c: Coincident(g11,g4)
    c: InternalAlignment(g8,g11)
    c: InternalAlignment(g9,g11)
    c: InternalAlignment(g10,g11)
    c: InternalAlignment(g12,g11)
    c: InternalAlignment(g13,g11)
    c: Coincident(g17,g5)
    c: Weight(g14) = 1
    c: Equal(g14,g15)
    c: Equal(g14,g16)
    c: Coincident(g17,g3)
    c: InternalAlignment(g14,g17)
    c: InternalAlignment(g15,g17)
    c: InternalAlignment(g16,g17)
    c: InternalAlignment(g18,g17)
    c: InternalAlignment(g19,g17)
    c: Block(g7)
    c: Block(g17)
    c: Block(g11)
    c: Block(g6)
FEATURE [Part::Extrusion] Extrude003
  Base = -> Sketch002
  Dir = (0,0,1)
  DirMode = 2
  FaceMakerClass = Part::FaceMakerBullseye
  LengthFwd = 260
  LengthRev = 0
  Solid = true
  Symmetric = false
FEATURE [Part::Extrusion] Extrude
  Base = -> Sketch
  Dir = (0,0,1)
  DirMode = 2
  FaceMakerClass = Part::FaceMakerBullseye
  LengthFwd = 14
  LengthRev = 0
  Solid = true
  Symmetric = false
